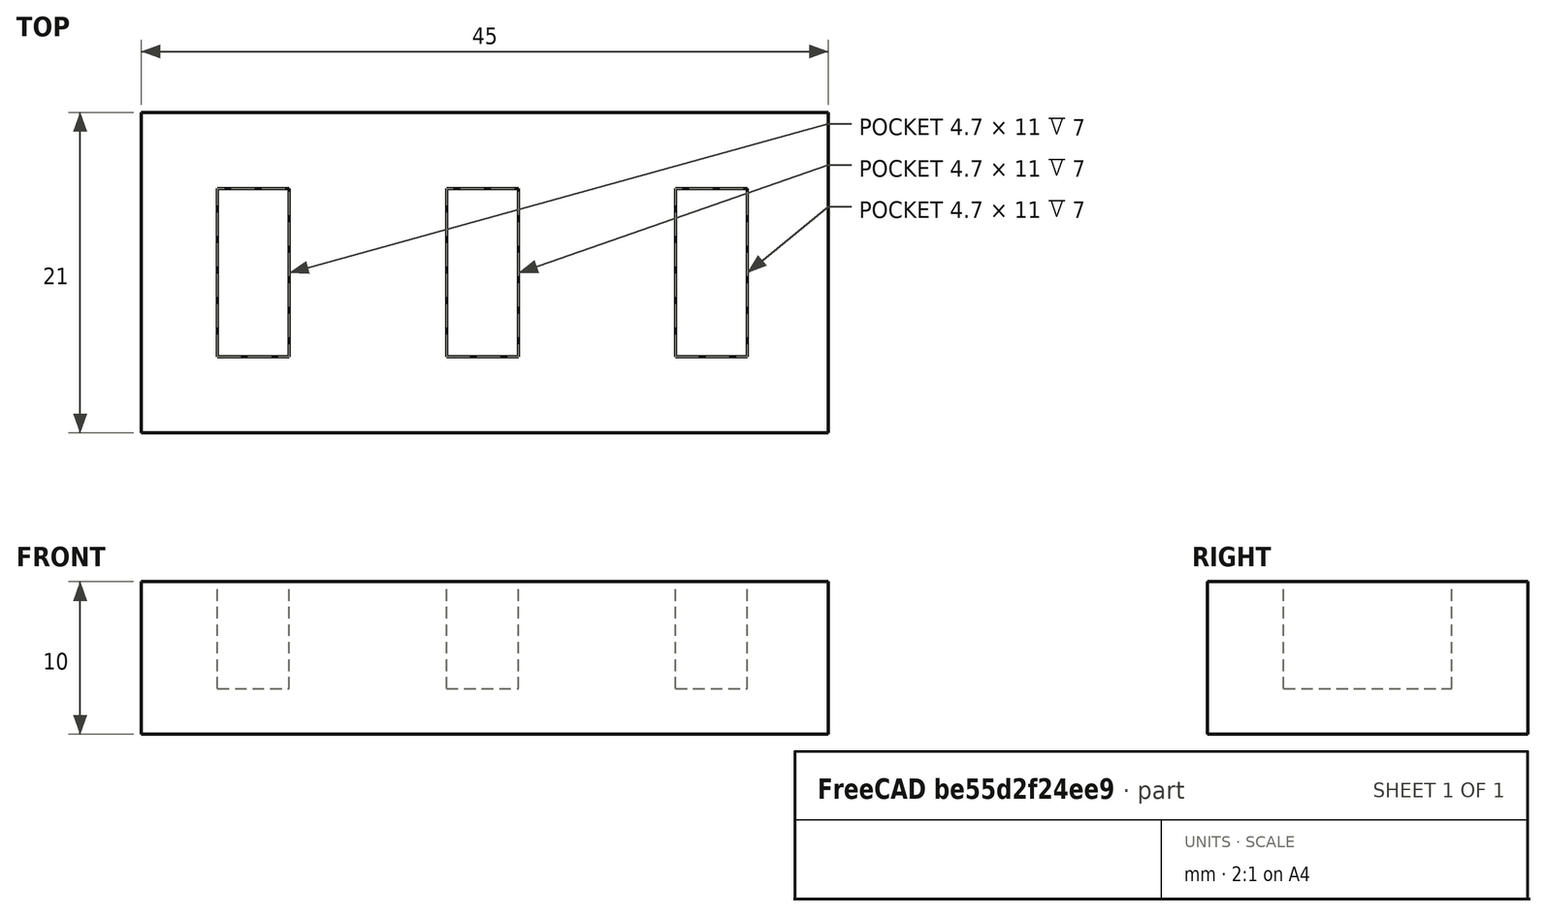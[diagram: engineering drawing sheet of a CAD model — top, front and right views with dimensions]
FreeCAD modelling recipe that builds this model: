
FCSTD DOCUMENT  (FreeCAD 1.0R39319 (Git))
Label: ojt1_t08p01_usb_flash
License: All rights reserved
LicenseURL: https://en.wikipedia.org/wiki/All_rights_reserved
objects: Part::Box×4, PartDesign::Body×1, Part::MultiFuse×1, Part::Cut×1
note: 7 computed .brp shape members not serialized (recipe doc carries the construction recipe); baked Part::Feature solids carry a one-line shape summary decoded from their .brp

FEATURE [PartDesign::Body] Body  label="objecte final"
  AllowCompound = false
  Origin = -> Origin
FEATURE [Part::Box] Box  label="ranura"
  AttacherType = Attacher::AttachEngine3D
  Height = 12
  Length = 4.7
  Width = 11
FEATURE [Part::Box] Box001  label="ranura001"
  AttacherType = Attacher::AttachEngine3D
  Height = 12
  Length = 4.7
  Placement = pos=(15,0,0) rot=(0,0,1;0rad)
  Width = 11
FEATURE [Part::Box] Box002  label="ranura002"
  AttacherType = Attacher::AttachEngine3D
  Height = 12
  Length = 4.7
  Placement = pos=(30,0,0) rot=(0,0,1;0rad)
  Width = 11
FEATURE [Part::MultiFuse] Fusion  label="ranures"
  Placement = pos=(5,5,3) rot=(0,0,1;0rad)
  Shapes = -> [Box,Box001,Box002]
FEATURE [Part::Box] Box003  label="base"
  AttacherType = Attacher::AttachEngine3D
  Height = 10
  Length = 45
  Width = 21
FEATURE [Part::Cut] Cut
  Base = -> Box003
  Tool = -> Fusion
